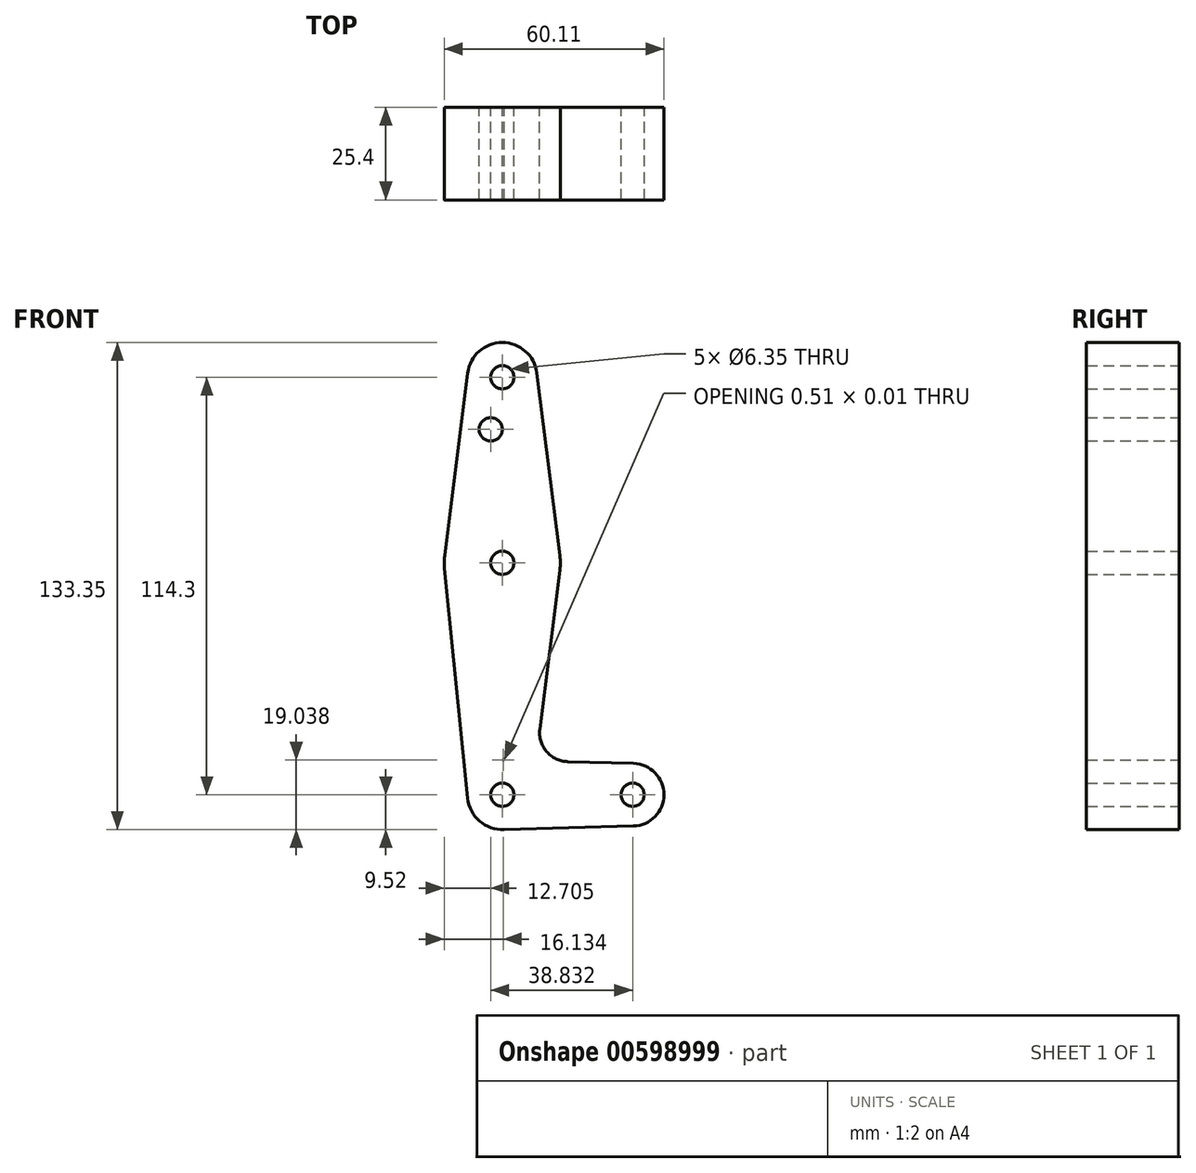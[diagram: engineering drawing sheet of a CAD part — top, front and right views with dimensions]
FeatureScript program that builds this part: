
annotation { "Feature Type Name" : "Feature", "Feature Type Description" : "" }
export const myFeature = defineFeature(function(context is Context, id is Id, definition is map)
    precondition{}
    {
        {
            var Q0;
            Q0=qCreatedBy(makeId("Front.planeOp"),FACE);
            var sketch = newSketch(context, id + "F0", { "sketchPlane" : qUnion([Q0])});
            skLineSegment(sketch, "E0", {"start": v(0, 114.3) * mm, "end": v(0, 0) * mm, "construction": true});
            skCircle(sketch, "E1", {"center": v(0, 114.3) * mm, "radius": 9.53 * mm});
            skCircle(sketch, "E2", {"center": v(0, 63.5) * mm, "radius": 15.88 * mm});
            skCircle(sketch, "E3", {"center": v(0, 0) * mm, "radius": 9.53 * mm});
            skPoint(sketch, "E4.center.orphan", {"position": v(30.76, 0) * mm});
            skPoint(sketch, "E5.orphan", {"position": v(35.66, 0) * mm});
            skLineSegment(sketch, "E6", {"start": v(0, 0) * mm, "end": v(35.66, 0) * mm, "construction": true});
            skCircle(sketch, "E7", {"center": v(35.66, 0) * mm, "radius": 8.57 * mm});
            skLineSegment(sketch, "E8", {"start": v(-9.45, 115.5) * mm, "end": v(-15.75, 65.48) * mm});
            skLineSegment(sketch, "E9", {"start": v(9.45, 115.5) * mm, "end": v(15.75, 65.48) * mm});
            skLineSegment(sketch, "E10", {"start": v(15.75, 61.52) * mm, "end": v(10.27, 17.99) * mm});
            skLineSegment(sketch, "E11", {"start": v(0, 9.53) * mm, "end": v(0.5, 9.51) * mm});
            skLineSegment(sketch, "E12", {"start": v(0, -9.53) * mm, "end": v(35.89, -8.57) * mm});
            skCircle(sketch, "E13", {"center": v(0, 114.3) * mm, "radius": 3.18 * mm});
            skCircle(sketch, "E14", {"center": v(0, 63.5) * mm, "radius": 3.18 * mm});
            skCircle(sketch, "E15", {"center": v(0, 0) * mm, "radius": 3.18 * mm});
            skCircle(sketch, "E16", {"center": v(35.66, 0) * mm, "radius": 3.18 * mm});
            skCircle(sketch, "E17", {"center": v(-3.17, 100.03) * mm, "radius": 3.18 * mm});
            skArc(sketch, "E18", {"start": v(10.27, 17.99) * mm, "mid": v(12.12, 11.82) * mm, "end": v(17.94, 9.05) * mm});
            skLineSegment(sketch, "E19.trimOffspring", {"start": v(17.94, 9.05) * mm, "end": v(35.89, 8.57) * mm});
            skPoint(sketch, "E20.end.orphan", {"position": v(-9.57, 0) * mm});
            skLineSegment(sketch, "E21", {"start": v(-9.48, -0.95) * mm, "end": v(-15.8, 61.91) * mm});
            skSolve(sketch);
        }
        {
            var Q0;
            Q0=qSketchRegion(id+"F0",true);
            extrude(context, id + "F1", {"entities" : qUnion([Q0]), "depth" : 3.05 * mm, "offsetDistance" : 25.4 * mm});
        }
        {
            var Q0;
            Q0=qSketchRegion(id+"F0",true);
            extrude(context, id + "F2", {"entities" : qUnion([Q0]), "operationType" : NewBodyOperationType.ADD, "depth" : 25.4 * mm, "offsetDistance" : 25.4 * mm});
        }
        {
            var Q0;
            Q0 = qSketchRegion(id + "F0", true);
            extrude(context, id + "F3", {"entities" : qUnion([Q0]), "operationType" : NewBodyOperationType.ADD, "depth" : 3.05 * mm, "offsetDistance" : 25.4 * mm});
        }
    });
